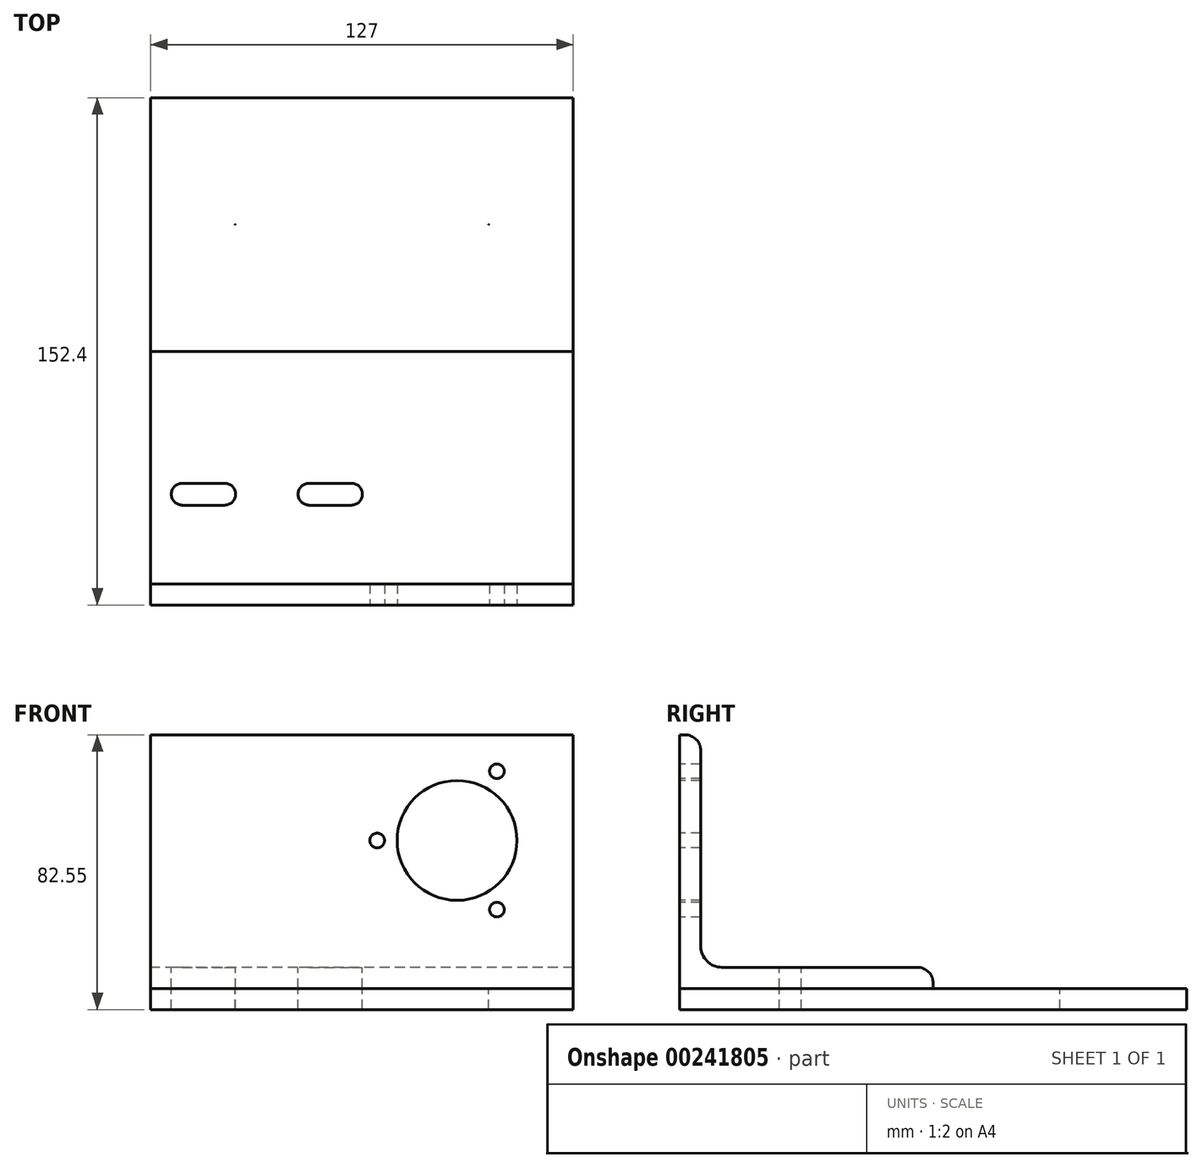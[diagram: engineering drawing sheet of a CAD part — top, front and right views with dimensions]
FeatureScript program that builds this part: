
annotation { "Feature Type Name" : "Feature", "Feature Type Description" : "" }
export const myFeature = defineFeature(function(context is Context, id is Id, definition is map)
    precondition{}
    {
        {
            var Q0;
            Q0=qCreatedBy(makeId("Top.planeOp"),FACE);
            var sketch = newSketch(context, id + "F0", { "sketchPlane" : qUnion([Q0])});
            skLineSegment(sketch, "E0.bottom", {"start": v(-63.5, 76.2) * mm, "end": v(63.5, 76.2) * mm});
            skLineSegment(sketch, "E0.top", {"start": v(-63.5, -76.2) * mm, "end": v(63.5, -76.2) * mm});
            skLineSegment(sketch, "E0.left", {"start": v(-63.5, 76.2) * mm, "end": v(-63.5, -76.2) * mm});
            skLineSegment(sketch, "E0.right", {"start": v(63.5, 76.2) * mm, "end": v(63.5, -76.2) * mm});
            skPoint(sketch, "E0.middle", {"position": v(0, 0) * mm});
            skSolve(sketch);
        }
        {
            var Q0;
            Q0 = qSketchRegion(id + "F0", true);
            extrude(context, id + "F1", {"entities" : qUnion([Q0]), "depth" : 6.35 * mm});
        }
        {
            var Q0;
            Q0=makeQuery(id+"F1.opExtrude","CAP_FACE",FACE,{"disambiguationData":[OSD([sQuery(id+"F0.wireOp",EDGE,"E0.bottom"),sQuery(id+"F0.wireOp",EDGE,"E0.top"),sQuery(id+"F0.wireOp",EDGE,"E0.left"),sQuery(id+"F0.wireOp",EDGE,"E0.right")])],"isStart":false});
            var sketch = newSketch(context, id + "F2", { "sketchPlane" : qUnion([Q0])});
            skLineSegment(sketch, "E1", {"start": v(-63.5, 38.1) * mm, "end": v(63.5, 38.1) * mm, "construction": true});
            skLineSegment(sketch, "E2", {"start": v(0, 81.83) * mm, "end": v(0, -85.09) * mm, "construction": true});
            skLineSegment(sketch, "E3.0", {"start": v(-38.1, 81.83) * mm, "end": v(-38.1, -85.09) * mm, "construction": true});
            skPoint(sketch, "E4", {"position": v(-38.1, 38.1) * mm});
            skPoint(sketch, "E5.MirrorP", {"position": v(38.1, 38.1) * mm});
            skSolve(sketch);
        }
        {
            var Q0;
            Q0=sQuery(id+"F2.wireOp",VERTEX,"E4");
            var Q1;
            Q1=sQuery(id+"F2.wireOp",VERTEX,"E5.MirrorP");
            var Q2;
            Q2=makeQuery(id+"F1.opExtrude","SWEPT_BODY",BODY,{"disambiguationData":[OSD([sQuery(id+"F0.wireOp",EDGE,"E0.bottom"),sQuery(id+"F0.wireOp",EDGE,"E0.top"),sQuery(id+"F0.wireOp",EDGE,"E0.left"),sQuery(id+"F0.wireOp",EDGE,"E0.right")])]});
            hole(context, id + "F3", {"style" : HoleStyle.SIMPLE, "endStyle" : HoleEndStyle.BLIND, "standardTappedOrClearance" : lookupTablePath({ "standard" : "ANSI", "size" : "17/64 (0.27)", "type" : "Drilled" }), "standardBlindInLast" : lookupTablePath({ "standard" : "ANSI", "size" : "17/64", "type" : "Drilled" }), "holeDiameter" : 17 / 1625.6 * mm, "holeDepth" : 10 * mm, "locations" : qUnion([Q0, Q1]), "scope" : qUnion([Q2])});
        }
        {
            var Q0;
            Q0=makeQuery(id+"F1.opExtrude","CAP_FACE",FACE,{"disambiguationData":[OSD([sQuery(id+"F0.wireOp",EDGE,"E0.bottom"),sQuery(id+"F0.wireOp",EDGE,"E0.top"),sQuery(id+"F0.wireOp",EDGE,"E0.left"),sQuery(id+"F0.wireOp",EDGE,"E0.right")])],"isStart":false});
            var sketch = newSketch(context, id + "F4", { "sketchPlane" : qUnion([Q0])});
            skLineSegment(sketch, "E6.0", {"start": v(-63.5, -76.2) * mm, "end": v(63.5, -76.2) * mm, "construction": true});
            skLineSegment(sketch, "E7.0", {"start": v(-63.5, -42.93) * mm, "end": v(63.5, -42.93) * mm, "construction": true});
            skLineSegment(sketch, "E8.0", {"start": v(-63.5, 76.2) * mm, "end": v(-63.5, -76.2) * mm, "construction": true});
            skLineSegment(sketch, "E9.0", {"start": v(-47.62, 76.2) * mm, "end": v(-47.63, -76.2) * mm, "construction": true});
            skLineSegment(sketch, "E10.0", {"start": v(-9.52, 76.2) * mm, "end": v(-9.53, -76.2) * mm, "construction": true});
            skPoint(sketch, "E11", {"position": v(-47.63, -42.93) * mm});
            skPoint(sketch, "E12", {"position": v(-9.53, -42.93) * mm});
            skSolve(sketch);
        }
        {
            var Q0;
            Q0=sQuery(id+"F4.wireOp",VERTEX,"E11");
            var Q1;
            Q1=sQuery(id+"F4.wireOp",VERTEX,"E12");
            var Q2;
            Q2=makeQuery(id+"F1.opExtrude","SWEPT_BODY",BODY,{"disambiguationData":[OSD([sQuery(id+"F0.wireOp",EDGE,"E0.bottom"),sQuery(id+"F0.wireOp",EDGE,"E0.top"),sQuery(id+"F0.wireOp",EDGE,"E0.left"),sQuery(id+"F0.wireOp",EDGE,"E0.right")])]});
            hole(context, id + "F5", {"style" : HoleStyle.SIMPLE, "endStyle" : HoleEndStyle.BLIND, "standardTappedOrClearance" : lookupTablePath({ "standard" : "ANSI", "engagement" : "75%", "pitch" : "24 tpi", "size" : "#10", "type" : "Tapped" }), "standardBlindInLast" : lookupTablePath({ "standard" : "ANSI", "engagement" : "75%", "pitch" : "24 tpi", "size" : "#10", "type" : "Tapped" }), "holeDiameter" : 3.8 * mm, "holeDepth" : 10 * mm, "locations" : qUnion([Q0, Q1]), "scope" : qUnion([Q2]), "majorDiameter" : 4.83 * mm});
        }
        {
            var Q0;
            Q0=qCreatedBy(makeId("Right.planeOp"),FACE);
            var sketch = newSketch(context, id + "F6", { "sketchPlane" : qUnion([Q0])});
            skLineSegment(sketch, "E13.0", {"start": v(76.2, 6.35) * mm, "end": v(-76.2, 6.35) * mm, "construction": true});
            skLineSegment(sketch, "E14.bottom", {"start": v(-76.2, 6.35) * mm, "end": v(0, 6.35) * mm});
            skLineSegment(sketch, "E14.top", {"start": v(-76.2, 82.55) * mm, "end": v(-74.68, 82.55) * mm});
            skLineSegment(sketch, "E14.left", {"start": v(-76.2, 6.35) * mm, "end": v(-76.2, 82.55) * mm});
            skLineSegment(sketch, "E14.right", {"start": v(0, 6.35) * mm, "end": v(0, 7.87) * mm});
            skLineSegment(sketch, "E15.0", {"start": v(-4.83, 12.7) * mm, "end": v(-63.5, 12.7) * mm});
            skLineSegment(sketch, "E16.0", {"start": v(-69.85, 19.05) * mm, "end": v(-69.85, 77.72) * mm});
            skArc(sketch, "E17.filletArc", {"start": v(-69.85, 19.05) * mm, "mid": v(-68, 14.56) * mm, "end": v(-63.5, 12.7) * mm});
            skArc(sketch, "E18.filletArc", {"start": v(-69.85, 77.72) * mm, "mid": v(-71.26, 81.14) * mm, "end": v(-74.68, 82.55) * mm});
            skArc(sketch, "E19.filletArc", {"start": v(0, 7.87) * mm, "mid": v(-1.41, 11.29) * mm, "end": v(-4.83, 12.7) * mm});
            skSolve(sketch);
        }
        {
            var Q0;
            Q0=makeQuery(id+"F6.imprint","IMPRINT",FACE,{"disambiguationData":[TD([[makeQuery(id+"F6.imprint","IMPRINT",EDGE,{"derivedFrom":sQuery(id+"F6.wireOp",EDGE,"E14.bottom")}),1.0]])]});
            extrude(context, id + "F7", {"entities" : qUnion([Q0]), "endBound" : BoundingType.SYMMETRIC, "depth" : 127 * mm});
        }
        {
            var Q0;
            Q0=makeQuery(id+"F7.opExtrude","SWEPT_FACE",FACE,{"disambiguationData":[OSD([sQuery(id+"F6.wireOp",EDGE,"E15.0")])]});
            var sketch = newSketch(context, id + "F8", { "sketchPlane" : qUnion([Q0])});
            skCircle(sketch, "E20.0", {"center": v(-9.53, -42.93) * mm, "radius": 1.9 * mm, "construction": true});
            skCircle(sketch, "E21.0", {"center": v(-47.63, -42.93) * mm, "radius": 1.9 * mm, "construction": true});
            skLineSegment(sketch, "E22", {"start": v(-47.63, -42.93) * mm, "end": v(-53.98, -42.93) * mm, "construction": true});
            skLineSegment(sketch, "E23", {"start": v(-53.98, -42.93) * mm, "end": v(-41.28, -42.93) * mm, "construction": true});
            skArc(sketch, "E24", {"start": v(-53.98, -39.62) * mm, "mid": v(-57.28, -42.93) * mm, "end": v(-53.98, -46.23) * mm});
            skArc(sketch, "E25", {"start": v(-41.28, -46.23) * mm, "mid": v(-37.97, -42.93) * mm, "end": v(-41.28, -39.62) * mm});
            skLineSegment(sketch, "E26", {"start": v(-53.98, -39.62) * mm, "end": v(-41.28, -39.62) * mm});
            skLineSegment(sketch, "E27.MirrorCS", {"start": v(-53.98, -46.23) * mm, "end": v(-41.28, -46.23) * mm});
            skLineSegment(sketch, "E28.1.0.0", {"start": v(-15.88, -42.93) * mm, "end": v(-3.18, -42.93) * mm, "construction": true});
            skLineSegment(sketch, "E28.1.0.2", {"start": v(-15.88, -39.62) * mm, "end": v(-3.18, -39.62) * mm});
            skLineSegment(sketch, "E28.1.0.3", {"start": v(-15.88, -46.23) * mm, "end": v(-3.18, -46.23) * mm});
            skArc(sketch, "E28.1.0.4", {"start": v(-15.88, -39.62) * mm, "mid": v(-19.18, -42.93) * mm, "end": v(-15.88, -46.23) * mm});
            skArc(sketch, "E28.1.0.5", {"start": v(-3.18, -46.23) * mm, "mid": v(0.13, -42.93) * mm, "end": v(-3.18, -39.62) * mm});
            skLineSegment(sketch, "E28.1.0.6", {"start": v(-9.53, -42.93) * mm, "end": v(-15.88, -42.93) * mm, "construction": true});
            skLineSegment(sketch, "E28.direction1", {"start": v(-53.98, -46.23) * mm, "end": v(-15.88, -46.23) * mm, "construction": true});
            skSolve(sketch);
        }
        {
            var Q0;
            Q0 = qSketchRegion(id + "F8", true);
            extrude(context, id + "F9", {"entities" : qUnion([Q0]), "operationType" : NewBodyOperationType.REMOVE, "endBound" : BoundingType.THROUGH_ALL, "oppositeDirection" : true, "depth" : 25.4 * mm});
        }
        {
            var Q0;
            Q0=makeQuery(id+"F7.opExtrude","SWEPT_FACE",FACE,{"disambiguationData":[OSD([sQuery(id+"F6.wireOp",EDGE,"E14.left")])]});
            var sketch = newSketch(context, id + "F10", { "sketchPlane" : qUnion([Q0])});
            skLineSegment(sketch, "E29.0", {"start": v(-63.5, 6.35) * mm, "end": v(-63.5, 82.55) * mm, "construction": true});
            skLineSegment(sketch, "E30.0", {"start": v(28.57, 6.35) * mm, "end": v(28.57, 82.55) * mm, "construction": true});
            skLineSegment(sketch, "E31.0", {"start": v(63.5, 82.55) * mm, "end": v(-63.5, 82.55) * mm, "construction": true});
            skLineSegment(sketch, "E32.0", {"start": v(63.5, 50.8) * mm, "end": v(-63.5, 50.8) * mm, "construction": true});
            skCircle(sketch, "E33", {"center": v(28.57, 50.8) * mm, "radius": 18 * mm});
            skSolve(sketch);
        }
        {
            var Q0;
            Q0 = qSketchRegion(id + "F10", true);
            extrude(context, id + "F11", {"entities" : qUnion([Q0]), "operationType" : NewBodyOperationType.REMOVE, "oppositeDirection" : true, "depth" : 25 * mm});
        }
        {
            var Q0;
            Q0=makeQuery(id+"F7.opExtrude","SWEPT_FACE",FACE,{"disambiguationData":[OSD([sQuery(id+"F6.wireOp",EDGE,"E14.left")])]});
            var sketch = newSketch(context, id + "F12", { "sketchPlane" : qUnion([Q0])});
            skCircle(sketch, "E34.0", {"center": v(28.57, 50.8) * mm, "radius": 18 * mm, "construction": true});
            skCircle(sketch, "E35", {"center": v(28.57, 50.8) * mm, "radius": 24 * mm, "construction": true});
            skLineSegment(sketch, "E36", {"start": v(28.57, 50.8) * mm, "end": v(-23.5, 50.8) * mm, "construction": true});
            skPoint(sketch, "E37", {"position": v(4.57, 50.8) * mm});
            skPoint(sketch, "E38.1.0", {"position": v(40.57, 30.02) * mm});
            skPoint(sketch, "E38.2.0", {"position": v(40.58, 71.58) * mm});
            skSolve(sketch);
        }
        {
            var Q0;
            Q0=sQuery(id+"F12.wireOp",VERTEX,"E37");
            var Q1;
            Q1=sQuery(id+"F12.wireOp",VERTEX,"E38.2.0");
            var Q2;
            Q2=sQuery(id+"F12.wireOp",VERTEX,"E38.1.0");
            var Q3;
            Q3=makeQuery(id+"F7.opExtrude","SWEPT_BODY",BODY,{"disambiguationData":[OSD([sQuery(id+"F6.wireOp",EDGE,"E14.bottom"),sQuery(id+"F6.wireOp",EDGE,"E14.top"),sQuery(id+"F6.wireOp",EDGE,"E14.left"),sQuery(id+"F6.wireOp",EDGE,"E14.right"),sQuery(id+"F6.wireOp",EDGE,"E15.0"),sQuery(id+"F6.wireOp",EDGE,"E16.0"),sQuery(id+"F6.wireOp",EDGE,"E17.filletArc"),sQuery(id+"F6.wireOp",EDGE,"E18.filletArc"),sQuery(id+"F6.wireOp",EDGE,"E19.filletArc")])]});
            hole(context, id + "F13", {"style" : HoleStyle.SIMPLE, "endStyle" : HoleEndStyle.THROUGH, "standardTappedOrClearance" : lookupTablePath({ "standard" : "ISO", "fit" : "Normal", "size" : "M4", "type" : "Clearance" }), "standardBlindInLast" : lookupTablePath({ "fit" : "Standard", "standard" : "ISO", "size" : "M4", "type" : "Clearance" }), "holeDiameter" : 4.4 * mm, "locations" : qUnion([Q0, Q1, Q2]), "scope" : qUnion([Q3]), "isTappedThrough" : true});
        }
    });
